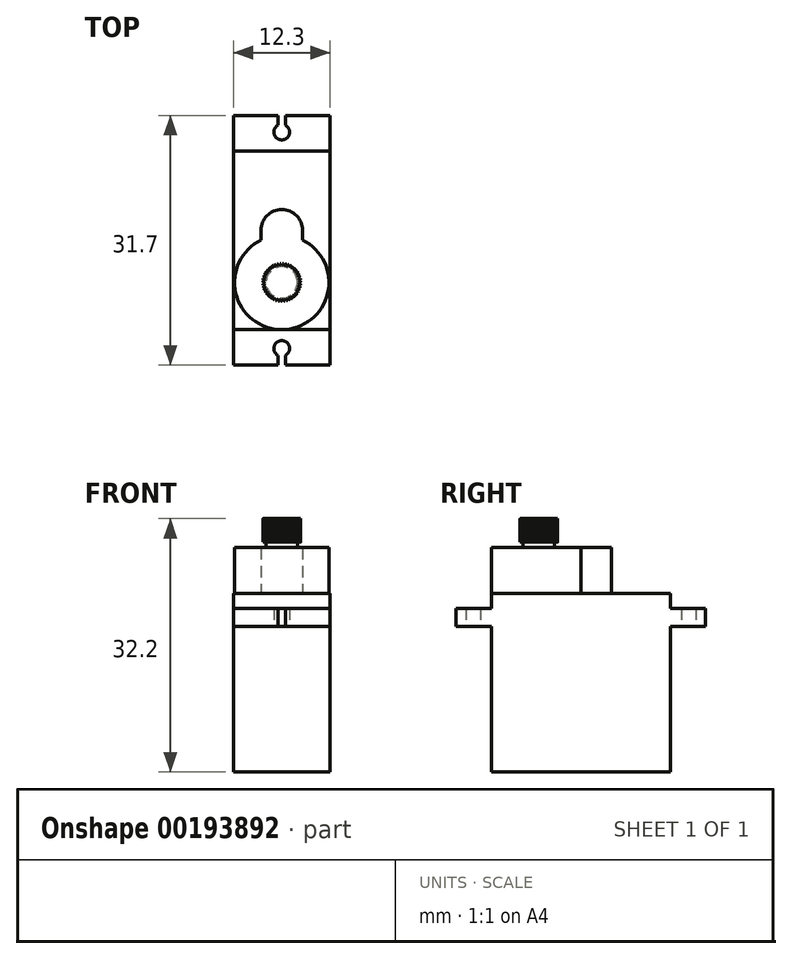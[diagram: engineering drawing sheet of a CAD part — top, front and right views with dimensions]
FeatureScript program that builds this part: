
annotation { "Feature Type Name" : "Feature", "Feature Type Description" : "" }
export const myFeature = defineFeature(function(context is Context, id is Id, definition is map)
    precondition{}
    {
        {
            var Q0;
            Q0=qCreatedBy(makeId("Front.planeOp"),FACE);
            cPlane(context, id + "F0", {"entities" : qUnion([Q0]), "cplaneType" : CPlaneType.OFFSET, "offset" : 70 * mm, "width" : 150 * mm, "height" : 150 * mm});
        }
        {
            var Q0;
            Q0=qCreatedBy(id+"F0.planeOp",FACE);
            var sketch = newSketch(context, id + "F1", { "sketchPlane" : qUnion([Q0])});
            skLineSegment(sketch, "E0.bottom", {"start": v(6.15, -9.25) * mm, "end": v(-6.15, -9.25) * mm});
            skLineSegment(sketch, "E0.top", {"start": v(6.15, 9.25) * mm, "end": v(-6.15, 9.25) * mm});
            skLineSegment(sketch, "E0.left", {"start": v(6.15, -9.25) * mm, "end": v(6.15, 9.25) * mm});
            skLineSegment(sketch, "E0.right", {"start": v(-6.15, -9.25) * mm, "end": v(-6.15, 9.25) * mm});
            skPoint(sketch, "E0.middle", {"position": v(0, 0) * mm});
            skSolve(sketch);
        }
        {
            var Q0;
            Q0=qSketchRegion(id+"F1",true);
            extrude(context, id + "F2", {"entities" : qUnion([Q0]), "depth" : 22.7 * mm});
        }
        {
            var Q0;
            Q0=makeQuery(id+"F2.opExtrude","SWEPT_FACE",FACE,{"disambiguationData":[OSD([sQuery(id+"F1.wireOp",EDGE,"E0.top")])]});
            var sketch = newSketch(context, id + "F3", { "sketchPlane" : qUnion([Q0])});
            skLineSegment(sketch, "E1.0", {"start": v(6.15, -70) * mm, "end": v(-6.15, -70) * mm});
            skLineSegment(sketch, "E2.0", {"start": v(-6.15, -92.7) * mm, "end": v(-6.15, -70) * mm});
            skLineSegment(sketch, "E3.0", {"start": v(6.15, -92.7) * mm, "end": v(6.15, -70) * mm});
            skLineSegment(sketch, "E4.0", {"start": v(6.15, -92.7) * mm, "end": v(-6.15, -92.7) * mm});
            skLineSegment(sketch, "E5.top", {"start": v(6.15, -65.5) * mm, "end": v(-6.15, -65.5) * mm});
            skLineSegment(sketch, "E5.left", {"start": v(6.15, -70) * mm, "end": v(6.15, -65.5) * mm});
            skLineSegment(sketch, "E5.right", {"start": v(-6.15, -70) * mm, "end": v(-6.15, -65.5) * mm});
            skLineSegment(sketch, "E6", {"start": v(6.15, -81.35) * mm, "end": v(-6.15, -81.35) * mm, "construction": true});
            skCircle(sketch, "E7", {"center": v(0, -67.6) * mm, "radius": 1 * mm});
            skLineSegment(sketch, "E8.MirrorCS", {"start": v(-6.15, -92.7) * mm, "end": v(-6.15, -97.2) * mm});
            skLineSegment(sketch, "E9.MirrorCS", {"start": v(6.15, -97.2) * mm, "end": v(-6.15, -97.2) * mm});
            skCircle(sketch, "E10.MirrorC", {"center": v(0, -95.1) * mm, "radius": 1 * mm});
            skLineSegment(sketch, "E11.MirrorCS", {"start": v(6.15, -92.7) * mm, "end": v(6.15, -97.2) * mm});
            skSolve(sketch);
        }
        {
            var Q0;
            Q0=qSketchRegion(id+"F3",true);
            extrude(context, id + "F4", {"entities" : qUnion([Q0]), "operationType" : NewBodyOperationType.ADD, "depth" : 2.3 * mm});
        }
        {
            var Q0;
            Q0=makeQuery(id+"F4.opExtrude","CAP_FACE",FACE,{"disambiguationData":[OSD([sQuery(id+"F3.wireOp",EDGE,"E2.0"),sQuery(id+"F3.wireOp",EDGE,"E3.0"),sQuery(id+"F3.wireOp",EDGE,"E5.top"),sQuery(id+"F3.wireOp",EDGE,"E5.left"),sQuery(id+"F3.wireOp",EDGE,"E5.right"),sQuery(id+"F3.wireOp",EDGE,"E7"),sQuery(id+"F3.wireOp",EDGE,"E8.MirrorCS"),sQuery(id+"F3.wireOp",EDGE,"E9.MirrorCS"),sQuery(id+"F3.wireOp",EDGE,"E10.MirrorC"),sQuery(id+"F3.wireOp",EDGE,"E11.MirrorCS")])],"isStart":false});
            var sketch = newSketch(context, id + "F5", { "sketchPlane" : qUnion([Q0])});
            skLineSegment(sketch, "E12.0", {"start": v(6.15, -81.35) * mm, "end": v(-6.15, -81.35) * mm});
            skLineSegment(sketch, "E13.bottom", {"start": v(0.5, -67.15) * mm, "end": v(-0.5, -67.15) * mm});
            skLineSegment(sketch, "E13.top", {"start": v(0.5, -63.85) * mm, "end": v(-0.5, -63.85) * mm});
            skLineSegment(sketch, "E13.left", {"start": v(0.5, -67.15) * mm, "end": v(0.5, -63.85) * mm});
            skLineSegment(sketch, "E13.right", {"start": v(-0.5, -67.15) * mm, "end": v(-0.5, -63.85) * mm});
            skPoint(sketch, "E13.middle", {"position": v(0, -65.5) * mm});
            skLineSegment(sketch, "E14.MirrorCS", {"start": v(0.5, -95.55) * mm, "end": v(-0.5, -95.55) * mm});
            skLineSegment(sketch, "E15.MirrorCS", {"start": v(-0.5, -95.55) * mm, "end": v(-0.5, -98.85) * mm});
            skLineSegment(sketch, "E16.MirrorCS", {"start": v(0.5, -95.55) * mm, "end": v(0.5, -98.85) * mm});
            skLineSegment(sketch, "E17.MirrorCS", {"start": v(0.5, -98.85) * mm, "end": v(-0.5, -98.85) * mm});
            skSolve(sketch);
        }
        {
            var Q0;
            Q0=qSketchRegion(id+"F5",true);
            extrude(context, id + "F6", {"entities" : qUnion([Q0]), "operationType" : NewBodyOperationType.REMOVE, "endBound" : BoundingType.THROUGH_ALL, "oppositeDirection" : true, "depth" : 25 * mm});
        }
        {
            var Q0;
            Q0=makeQuery(id+"F4.opExtrude","CAP_FACE",FACE,{"disambiguationData":[OSD([sQuery(id+"F3.wireOp",EDGE,"E2.0"),sQuery(id+"F3.wireOp",EDGE,"E3.0"),sQuery(id+"F3.wireOp",EDGE,"E5.top"),sQuery(id+"F3.wireOp",EDGE,"E5.left"),sQuery(id+"F3.wireOp",EDGE,"E5.right"),sQuery(id+"F3.wireOp",EDGE,"E7"),sQuery(id+"F3.wireOp",EDGE,"E8.MirrorCS"),sQuery(id+"F3.wireOp",EDGE,"E9.MirrorCS"),sQuery(id+"F3.wireOp",EDGE,"E10.MirrorC"),sQuery(id+"F3.wireOp",EDGE,"E11.MirrorCS")])],"isStart":false});
            var sketch = newSketch(context, id + "F7", { "sketchPlane" : qUnion([Q0])});
            skLineSegment(sketch, "E18.0", {"start": v(6.15, -92.7) * mm, "end": v(-6.15, -92.7) * mm});
            skLineSegment(sketch, "E19.0", {"start": v(6.15, -70) * mm, "end": v(-6.15, -70) * mm});
            skLineSegment(sketch, "E20.bottom", {"start": v(-6.15, -92.7) * mm, "end": v(6.15, -92.7) * mm});
            skLineSegment(sketch, "E20.top", {"start": v(-6.15, -70) * mm, "end": v(6.15, -70) * mm});
            skLineSegment(sketch, "E20.left", {"start": v(-6.15, -92.7) * mm, "end": v(-6.15, -70) * mm});
            skLineSegment(sketch, "E20.right", {"start": v(6.15, -92.7) * mm, "end": v(6.15, -70) * mm});
            skSolve(sketch);
        }
        {
            var Q0;
            Q0=qSketchRegion(id+"F7",true);
            extrude(context, id + "F8", {"entities" : qUnion([Q0]), "operationType" : NewBodyOperationType.ADD, "depth" : 1.9 * mm});
        }
        {
            var Q0;
            Q0=makeQuery(id+"F8.opExtrude","CAP_FACE",FACE,{"disambiguationData":[OSD([sQuery(id+"F7.wireOp",EDGE,"E20.bottom"),sQuery(id+"F7.wireOp",EDGE,"E20.top"),sQuery(id+"F7.wireOp",EDGE,"E20.left"),sQuery(id+"F7.wireOp",EDGE,"E20.right")])],"isStart":false});
            var sketch = newSketch(context, id + "F9", { "sketchPlane" : qUnion([Q0])});
            skArc(sketch, "E21.0", {"start": v(-0.5, -95.97) * mm, "mid": v(0, -94.1) * mm, "end": v(0.5, -95.97) * mm});
            skCircle(sketch, "E22", {"center": v(0, -86.7) * mm, "radius": 6 * mm});
            skLineSegment(sketch, "E23.0", {"start": v(-6.15, -92.7) * mm, "end": v(6.15, -92.7) * mm});
            skArc(sketch, "E24", {"start": v(2.65, -80.1) * mm, "mid": v(0, -77.45) * mm, "end": v(-2.65, -80.1) * mm});
            skPoint(sketch, "E24.centerSnap0", {"position": v(0, -92.7) * mm});
            skLineSegment(sketch, "E25", {"start": v(-2.65, -80.1) * mm, "end": v(-2.65, -81.32) * mm});
            skLineSegment(sketch, "E26", {"start": v(2.65, -80.1) * mm, "end": v(2.65, -81.32) * mm});
            skSolve(sketch);
        }
        {
            var Q0;
            Q0=qSketchRegion(id+"F9",true);
            extrude(context, id + "F10", {"entities" : qUnion([Q0]), "operationType" : NewBodyOperationType.ADD, "depth" : 5.8 * mm});
        }
        {
            var Q0;
            Q0=makeQuery(id+"F10.opExtrude","CAP_FACE",FACE,{"disambiguationData":[OSD([sQuery(id+"F9.wireOp",EDGE,"E22"),sQuery(id+"F9.wireOp",EDGE,"E24"),sQuery(id+"F9.wireOp",EDGE,"E25"),sQuery(id+"F9.wireOp",EDGE,"E26")])],"isStart":false});
            var sketch = newSketch(context, id + "F11", { "sketchPlane" : qUnion([Q0])});
            skArc(sketch, "E27.0", {"start": v(-0.5, -95.97) * mm, "mid": v(0, -94.1) * mm, "end": v(0.5, -95.97) * mm});
            skArc(sketch, "E28.0", {"start": v(-2.65, -81.32) * mm, "mid": v(0, -92.7) * mm, "end": v(2.65, -81.32) * mm});
            skCircle(sketch, "E29", {"center": v(0, -86.7) * mm, "radius": 2 * mm});
            skSolve(sketch);
        }
        {
            var Q0;
            Q0=qSketchRegion(id+"F11",true);
            extrude(context, id + "F12", {"entities" : qUnion([Q0]), "depth" : 0.7 * mm});
        }
        {
            var Q0;
            Q0=makeQuery(id+"F12.opExtrude","CAP_FACE",FACE,{"disambiguationData":[OSD([sQuery(id+"F11.wireOp",EDGE,"E29")])],"isStart":false});
            var sketch = newSketch(context, id + "F13", { "sketchPlane" : qUnion([Q0])});
            skCircle(sketch, "E30.0", {"center": v(0, -86.7) * mm, "radius": 2 * mm});
            skCircle(sketch, "E31", {"center": v(0, -86.7) * mm, "radius": 2.4 * mm});
            skSolve(sketch);
        }
        {
            var Q0;
            Q0=makeQuery(id+"F13.imprint","IMPRINT",FACE,{"disambiguationData":[TD([[makeQuery(id+"F13.imprint","IMPRINT",EDGE,{"derivedFrom":sQuery(id+"F13.wireOp",EDGE,"E30.0")}),1.0]])]});
            var Q1;
            Q1=makeQuery(id+"F13.imprint","IMPRINT",FACE,{"disambiguationData":[TD([[makeQuery(id+"F13.imprint","IMPRINT",EDGE,{"derivedFrom":sQuery(id+"F13.wireOp",EDGE,"E30.0")}),-1.0]])]});
            extrude(context, id + "F14", {"entities" : qUnion([Q0, Q1]), "operationType" : NewBodyOperationType.ADD, "depth" : 3 * mm});
        }
        {
            var Q0;
            Q0=makeQuery(id+"F14.opExtrude","CAP_FACE",FACE,{"disambiguationData":[OSD([sQuery(id+"F13.wireOp",EDGE,"E31")])],"isStart":false});
            var sketch = newSketch(context, id + "F15", { "sketchPlane" : qUnion([Q0])});
            skLineSegment(sketch, "E32", {"start": v(1.26, -84.59) * mm, "end": v(1.13, -84.9) * mm});
            skLineSegment(sketch, "E33", {"start": v(1.13, -84.9) * mm, "end": v(1.48, -84.73) * mm});
            skLineSegment(sketch, "E34", {"start": v(1.48, -84.73) * mm, "end": v(1.26, -84.59) * mm});
            skCircle(sketch, "E35.0.0", {"center": v(0, -86.7) * mm, "radius": 2.4 * mm});
            skSolve(sketch);
        }
        {
            var Q0;
            {var subQ0=sQuery(id+"F15.wireOp",EDGE,"E34");Q0=makeQuery(id+"F15.imprint","IMPRINT",FACE,{"disambiguationData":[TD([[makeQuery(id+"F15.imprint","IMPRINT",EDGE,{"derivedFrom":subQ0}),1.0]])]});}
            var Q1;
            {var subQ0=sQuery(id+"F15.wireOp",EDGE,"E33");var subQ1=sQuery(id+"F15.wireOp",EDGE,"E32");var subQ2=makeQuery(id+"F15.imprint","INTERSECT",VERTEX,{"derivedFrom":[subQ1,subQ0]});Q1=makeQuery(id+"F15.imprint","IMPRINT",FACE,{"disambiguationData":[TD([[makeQuery(id+"F15.imprint","IMPRINT",EDGE,{"disambiguationData":[TD([[subQ2,1.0]])],"derivedFrom":subQ1}),1.0]])]});}
            extrude(context, id + "F16", {"entities" : qUnion([Q0, Q1]), "endBound" : BoundingType.UP_TO_NEXT, "oppositeDirection" : true, "depth" : 5 * mm});
        }
        {
            var Q0;
            Q0=makeQuery(id+"F16.opExtrude","SWEPT_BODY",BODY,{"disambiguationData":[OSD([sQuery(id+"F15.wireOp",EDGE,"E32"),sQuery(id+"F15.wireOp",EDGE,"E33"),sQuery(id+"F15.wireOp",EDGE,"E34")])]});
            var Q1;
            Q1=makeQuery(id+"F14.opExtrude","CAP_EDGE",EDGE,{"disambiguationData":[OSD([sQuery(id+"F13.wireOp",EDGE,"E31")])],"isStart":false});
            circularPattern(context, id + "F17", {"operationType" : NewBodyOperationType.REMOVE, "entities" : qUnion([Q0]), "axis" : qUnion([Q1]), "angle" : 360 * degree, "instanceCount" : 43, "equalSpace" : true});
        }
    });
